# Revit family: Contour - Bevel Large
name_source: partatom
category: Lighting Fixtures
revit_build: Autodesk Revit 2014 (Build: 20140709_2115(x64)
units: mm (PartAtom-declared; Revit-internal decimal feet)

## types (1)
- 20-3/4"Dia x 20-3/4"H
    Adjustable Suspension Height = 48"
    Cables = 1/16" Stainless Steel Cable
    Canopy Type = Powder Coat White
    Color Filter = 16777215
    Dia = 20 3/4"
    Diffuser = White Opal Acrylic
    Dimming Compatibility = No
    Dimming Lamp Color Temperature Shift = <None>
    Driver = -
    Hardware = <By Category>
    Height = 20 3/4"
    Input = 120v
    Intensity = LED System
    Lid = Removable powder coated
    Light Source Symbol Size = 8"
    Manufacturer = LightArt
    Material Options = http://www.3-form.com
http://www.3-form.com
    Model = BEVEL
    Shade = 1/8" VARIA
    Standards = 6-8 week lead time
    Type Comments = Does not include lamp
Does not include lamp
    URL = http://lightart.com
    Wattage Comments = 14

## geometry (parser evidence)
native form markers: Sweep x4
no freeform markers — native parametric forms only
